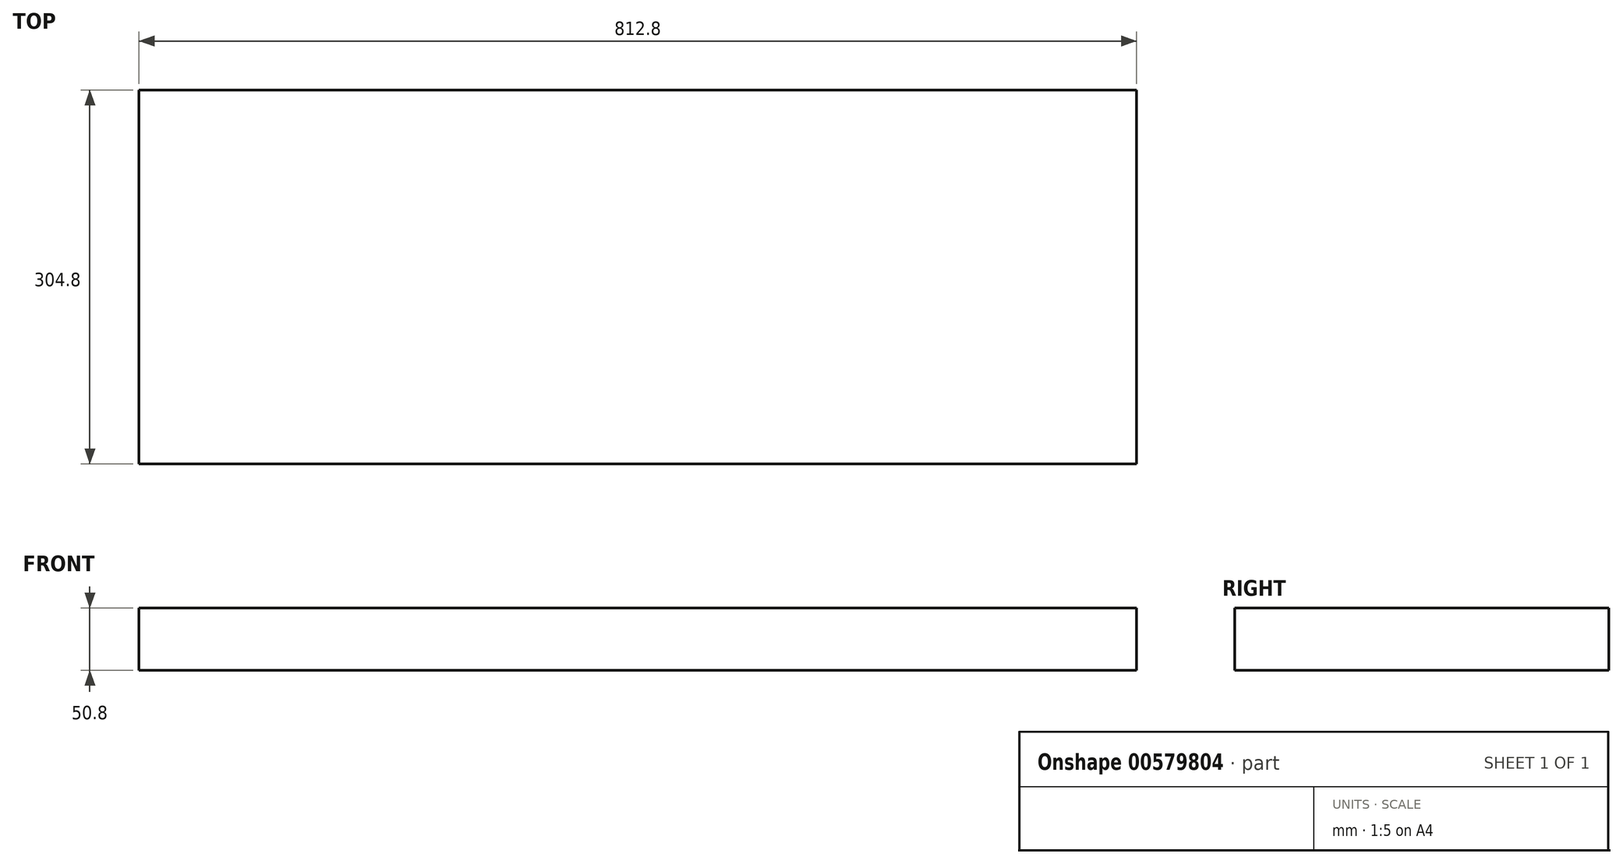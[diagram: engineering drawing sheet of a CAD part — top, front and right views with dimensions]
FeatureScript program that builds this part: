
annotation { "Feature Type Name" : "Feature", "Feature Type Description" : "" }
export const myFeature = defineFeature(function(context is Context, id is Id, definition is map)
    precondition{}
    {
        {
            var Q0;
            Q0=qCreatedBy(makeId("Top.planeOp"),FACE);
            var sketch = newSketch(context, id + "F0", { "sketchPlane" : qUnion([Q0])});
            skLineSegment(sketch, "E0.bottom", {"start": v(406.4, 152.4) * mm, "end": v(-406.4, 152.4) * mm});
            skLineSegment(sketch, "E0.top", {"start": v(406.4, -152.4) * mm, "end": v(-406.4, -152.4) * mm});
            skLineSegment(sketch, "E0.left", {"start": v(406.4, 152.4) * mm, "end": v(406.4, -152.4) * mm});
            skLineSegment(sketch, "E0.right", {"start": v(-406.4, 152.4) * mm, "end": v(-406.4, -152.4) * mm});
            skPoint(sketch, "E0.middle", {"position": v(0, 0) * mm});
            skSolve(sketch);
        }
        {
            var Q0;
            Q0=qSketchRegion(id+"F0",true);
            extrude(context, id + "F1", {"entities" : qUnion([Q0]), "depth" : 50.8 * mm, "offsetDistance" : 25.4 * mm});
        }
    });
